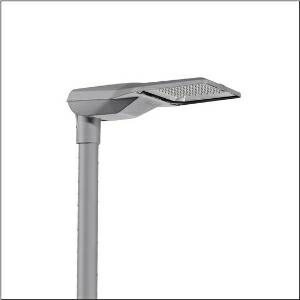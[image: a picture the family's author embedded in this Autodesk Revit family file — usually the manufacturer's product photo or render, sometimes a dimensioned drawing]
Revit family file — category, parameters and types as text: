
# Revit family: streetlight_sl_21_iq_midi___st0_5a_5xe3b41d08nb_db24
name_source: partatom
category: Lighting Fixtures
units: mm (PartAtom-declared; Revit-internal decimal feet)

## family parameters
Cut with Voids When Loaded = No
Host = Face
Light Source = No
Part Type = Normal
Room Calculation Point = No
Round Connector Dimension = Use Diameter
Shared = No

## types (1)
- --- (1 x LED, 24250 lm, 155.5 W, 4000K)
    Apparent Load = 155 VA
    CIE Flux Codes = 43 76 97 100 100
    Color Rendering = 70
    Color Temperature = 4000K
    Default Elevation = 1800 mm
    Description = Streetlight SL 21 iQ midi, mast luminaire, primary light control with lens, of PMMA, primary optical cover: cover, of toughened safety glass, transparent, light distribution: ST0.5a, light emission: direct distribution, primary light characteristic: asymmetric, installation type: post-top, side-entry, LED, High Power LED, rated luminous flux: 24.250lm, luminous efficacy: 156lm/W, light colour: 740, colour temperature: 4000K, control gear: iQ-Comfort, control: Auto-Match, Temp-Guard, Lumen-Switch, Night-Set, Smart-Wire, Light-Fading, Desk-Remote (wireless, voltage-free reading and setting of iQ features in the workshop via application-optimized NFC function/RFID function), optimised constant luminous flux control (CLO 2.0), pre-setting: linear dimming characteristic, mains connection: 230..240V, AC, 50/60Hz, start of lifetime: 156W, end of service life: 162W, reduction: 69W, luminaire housing, of diecast aluminium, powder-coated, SITECO metallic grey (DB 702S), corrosivity category C5 high according to DIN EN ISO 12944, please order mast flange separately, inclination adjustable: 0°, 5°, 10°, 15°, sealing non-destructively replaceable, multi-level sealing system, length: 644mm, width: 335mm, height: 110mm, mast flange for spigot size: 42mm (side-entry): 5XC10008XM4, 60/48mm (side-entry/post-top): 5XC10108XM2, 76/60mm (side-entry/post-top): 5XC10108XM1, mounting height: 4..8m, protection rating (complete): IP66, insulation class (complete): insulation class II (safety insulation), certification: CE, ENEC, ENEC+, VDE, impact resistance: IK10, permissible operating ambient temperature for outdoor applications: -40..+50°C, standard-compliant lighting for roads and squares, packaging unit: 1 piece

Light Distribution: ST0.5a
    Height = 111 mm
    Lamp = 1 x LED
    Lamp Light Flux = 24250 lm
    Lamp Power = 155.5 W
    Lamp count = 1
    Length = 644 mm
    Luminous efficacy = 156 lm/W
    Manufacturer = Siteco
    ModVariant = No
    Model = 5XE3B41D08NB
    Number of Poles = 1
    OnlyDefault = Yes
    Power Factor = 1
    Product Name = Streetlight SL 21 iQ midi | ST0.5a
    Product group = mast luminaire | pylon top
    ProductGroupID = 6100
    Protection Class = Protection class II
    Protection Degree = IP 66
    RLX_Detail_Level = 1
    RLX_Emergency_Light_Flux = 0 lm
    RLX_Emergency_Type = 0
    RLX_Emergency_Type_DB = No
    RlxData = <blob elided: 38377 chars, md5=09dad22e>
    Socket = socket
    Standby Power = 0 W
    System Light Flux = 24250 lm
    System Power = 155 W
    Type Comments = factory setting: luminous flux: 100 % | dim-lin: 254 | 823 mA
    Type Image = l_1004298.jpg
    URL = http://relux.com
    VarID = @adj_170983
    Voltage = 0 V
    Weight = 0.00 kg
    Width = 336 mm

## geometry (parser evidence)
native form markers: Blend x4, Sweep x11
no freeform markers — native parametric forms only
